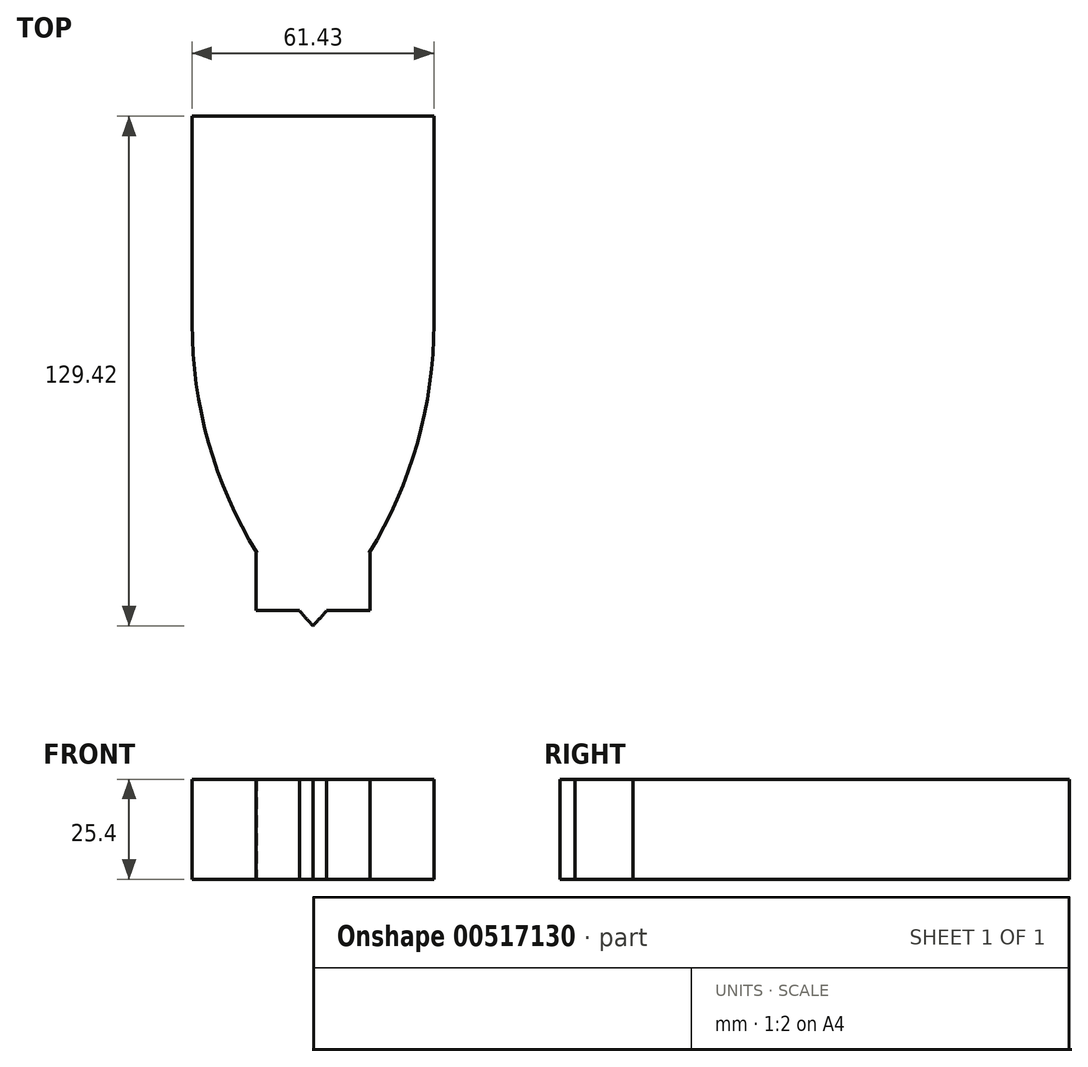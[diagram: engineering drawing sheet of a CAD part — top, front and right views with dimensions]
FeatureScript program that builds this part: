
annotation { "Feature Type Name" : "Feature", "Feature Type Description" : "" }
export const myFeature = defineFeature(function(context is Context, id is Id, definition is map)
    precondition{}
    {
        {
            var Q0;
            Q0=qCreatedBy(makeId("Top.planeOp"),FACE);
            var sketch = newSketch(context, id + "F0", { "sketchPlane" : qUnion([Q0])});
            skLineSegment(sketch, "E0", {"start": v(0, 52.74) * mm, "end": v(-61.43, 52.74) * mm});
            skLineSegment(sketch, "E1", {"start": v(-61.43, 52.74) * mm, "end": v(-61.43, 0) * mm});
            skLineSegment(sketch, "E2", {"start": v(-61.43, 0) * mm, "end": v(0, 0) * mm});
            skLineSegment(sketch, "E3", {"start": v(0, 0) * mm, "end": v(0, 52.74) * mm});
            skArc(sketch, "E4", {"start": v(-30.72, -76.68) * mm, "mid": v(-7.96, -41.3) * mm, "end": v(0, 0) * mm});
            skPoint(sketch, "E4.startSnap0", {"position": v(-30.72, 0) * mm});
            skLineSegment(sketch, "E5", {"start": v(-30.72, 0) * mm, "end": v(-30.72, -76.68) * mm});
            skArc(sketch, "E6.MirrorCS", {"start": v(-30.72, -76.68) * mm, "mid": v(-53.47, -41.3) * mm, "end": v(-61.43, 0) * mm});
            skLineSegment(sketch, "E7", {"start": v(0, 46.37) * mm, "end": v(12.7, 46.37) * mm});
            skLineSegment(sketch, "E8", {"start": v(-61.43, 46.37) * mm, "end": v(-74.13, 46.37) * mm});
            skLineSegment(sketch, "E9.bottom", {"start": v(-30.72, -58.17) * mm, "end": v(-16.28, -58.17) * mm});
            skLineSegment(sketch, "E9.top", {"start": v(-30.72, -72.85) * mm, "end": v(-16.28, -72.85) * mm});
            skLineSegment(sketch, "E9.left", {"start": v(-30.72, -58.17) * mm, "end": v(-30.72, -72.85) * mm});
            skLineSegment(sketch, "E9.right", {"start": v(-16.28, -58.17) * mm, "end": v(-16.28, -72.85) * mm});
            skLineSegment(sketch, "E10.MirrorCS", {"start": v(-30.72, -72.85) * mm, "end": v(-45.15, -72.85) * mm});
            skLineSegment(sketch, "E11.MirrorCS", {"start": v(-45.15, -58.17) * mm, "end": v(-45.15, -72.85) * mm});
            skLineSegment(sketch, "E12.MirrorCS", {"start": v(-30.72, -58.17) * mm, "end": v(-45.15, -58.17) * mm});
            skSolve(sketch);
        }
        {
            var Q0;
            Q0 = qSketchRegion(id + "F0", true);
            extrude(context, id + "F1", {"entities" : qUnion([Q0]), "depth" : 25.4 * mm, "offsetDistance" : 25.4 * mm});
        }
    });
